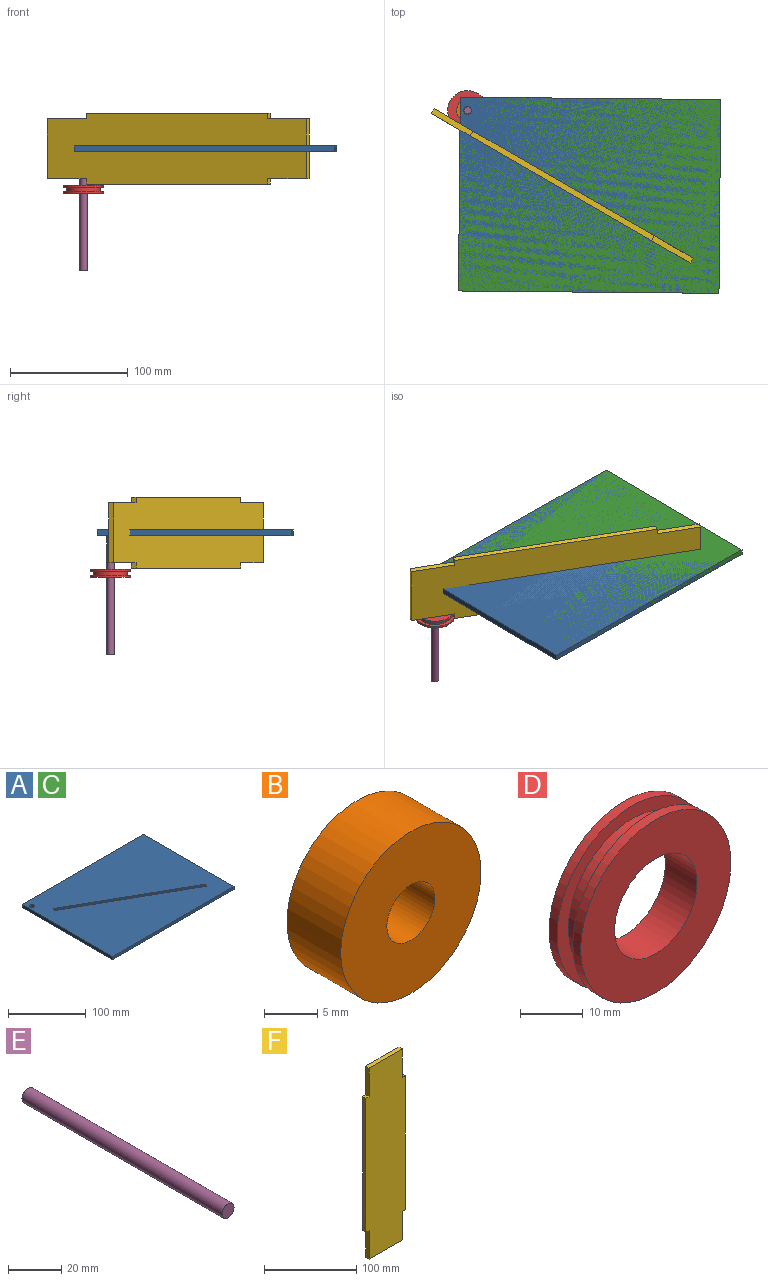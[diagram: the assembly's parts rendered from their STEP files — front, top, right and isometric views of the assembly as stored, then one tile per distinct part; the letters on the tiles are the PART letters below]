
ASSEMBLY  parts=6 mates=3
PART A: 11 faces, bbox 221.1x164.5x4.8 mm
  f0: plane 164.51x4.76mm, normal (1,0,0), area 783.5mm2, adj f1,f6,f9,f10
  f1: plane 221.11x4.76mm, normal (0,1,0), area 1053.1mm2, adj f0,f2,f9,f10
  f2: plane 164.51x4.76mm, normal (-1,0,0), area 783.5mm2, adj f1,f6,f9,f10
  f3: plane 4.76x4.15mm, normal (0.87,-0.49,0), area 22.7mm2, adj f4,f7,f9,f10
  f4: plane 176.89x100mm, normal (-0.49,-0.87,0), area 967.7mm2, adj f3,f5,f9,f10
  f5: plane 4.76x4.15mm, normal (-0.87,0.49,0), area 22.7mm2, adj f4,f7,f9,f10
  f6: plane 221.11x4.76mm, normal (0,-1,0), area 1053.1mm2, adj f0,f2,f9,f10
  f7: plane 176.89x100mm, normal (0.49,0.87,0), area 967.7mm2, adj f3,f5,f9,f10
  f8: cylinder r=3.17mm len=6.35mm, axis (0,0,-1), area 95mm2, adj f9,f10
  f9: plane 221.11x164.51mm, normal (0,0,1), area 35376.1mm2, adj f0,f1,f2,f3,f4,f5,f6,f7
  f10: plane 221.11x164.51mm, normal (0,0,-1), area 35376.1mm2, adj f0,f1,f2,f3,f4,f5,f6,f7
PART B: 4 faces, bbox 18.5x7.1x18.5 mm
  f0: cylinder r=3.17mm len=7.11mm, axis (0,1,0), area 141.9mm2, adj f2,f3
  f1: cylinder r=9.27mm len=18.54mm, axis (0,1,0), area 414.3mm2, adj f2,f3
  f2: plane 18.54x18.54mm, normal (0,-1,0), area 238.4mm2, adj f0,f1
  f3: plane 18.54x18.54mm, normal (0,1,0), area 238.4mm2, adj f0,f1
PART C: same geometry as A
PART D: 8 faces, bbox 33.8x7.1x33.8 mm
  f0: cylinder r=16.89mm len=33.78mm, axis (0,1,0), area 188.7mm2, adj f4,f7
  f1: cylinder r=9.27mm len=18.54mm, axis (0,1,0), area 414.3mm2, adj f3,f4
  f2: cylinder r=16.89mm len=33.78mm, axis (0,1,0), area 188.7mm2, adj f3,f6
  f3: plane 33.78x33.78mm, normal (0,-1,0), area 626.3mm2, adj f1,f2
  f4: plane 33.78x33.78mm, normal (0,1,0), area 626.3mm2, adj f0,f1
  f5: cylinder r=14.35mm len=28.7mm, axis (0,1,0), area 320.6mm2, adj f6,f7
  f6: plane 33.78x33.78mm, normal (0,1,0), area 249.3mm2, adj f2,f5
  f7: plane 33.78x33.78mm, normal (0,-1,0), area 249.3mm2, adj f0,f5
PART E: 3 faces, bbox 6.4x106x6.4 mm
  f0: cylinder r=3.17mm len=106.05mm, axis (0,1,0), area 2115.5mm2, adj f1,f2
  f1: plane 6.35x6.35mm, normal (0,-1,0), area 31.7mm2, adj f0
  f2: plane 6.35x6.35mm, normal (0,1,0), area 31.7mm2, adj f0
PART F: 14 faces, bbox 60.3x4.8x254 mm
  f0: plane 4.76x4.76mm, normal (0,0,-1), area 22.7mm2, adj f1,f11,f12,f13
  f1: plane 38.1x4.76mm, normal (-1,0,0), area 181.5mm2, adj f0,f2,f12,f13
  f2: plane 50.8x4.76mm, normal (0,0,-1), area 241.9mm2, adj f1,f3,f12,f13
  f3: plane 38.1x4.76mm, normal (1,0,0), area 181.5mm2, adj f2,f4,f12,f13
  f4: plane 4.76x4.76mm, normal (0,0,-1), area 22.7mm2, adj f3,f5,f12,f13
  f5: plane 177.8x4.76mm, normal (1,0,0), area 846.8mm2, adj f4,f6,f12,f13
  f6: plane 4.76x4.76mm, normal (0,0,1), area 22.7mm2, adj f5,f7,f12,f13
  f7: plane 38.1x4.76mm, normal (1,0,0), area 181.5mm2, adj f6,f8,f12,f13
  f8: plane 50.8x4.76mm, normal (0,0,1), area 241.9mm2, adj f7,f9,f12,f13
  f9: plane 38.1x4.76mm, normal (-1,0,0), area 181.5mm2, adj f8,f10,f12,f13
  f10: plane 4.76x4.76mm, normal (0,0,1), area 22.7mm2, adj f9,f11,f12,f13
  f11: plane 177.8x4.76mm, normal (-1,0,0), area 846.8mm2, adj f0,f10,f12,f13
  f12: plane 254x60.33mm, normal (0,-1,0), area 14596.7mm2, adj f0,f1,f2,f3,f4,f5,f6,f7
  f13: plane 254x60.33mm, normal (0,1,0), area 14596.7mm2, adj f0,f1,f2,f3,f4,f5,f6,f7
PLACE A rot(axis=(0,0,-1),0.5deg) t=(-457.49,-244.18,4.98)mm
PLACE B rot(axis=(-1,0,0),90deg) t=(-449.75,-90.96,-30.58)mm
PLACE C rot(axis=(0,0,-1),0.5deg) t=(-457.49,-244.18,4.98)mm
PLACE D rot(axis=(-1,0,0),90deg) t=(-449.75,-90.96,-30.58)mm
PLACE E rot(axis=(-1,0,0),90deg) t=(-449.75,-90.96,-96.31)mm
PLACE F rot(axis=(0.25,0.94,-0.25),93.8deg) t=(-445.2,-108.49,7.36)mm
MATE fastened D.f1 <-> B.f1  axis (0,0,-1) through (-449.75,-90.96,-30.58)mm
MATE cylindrical B.f0 <-> E.f0  axis (0,0,-1) through (-449.75,-90.96,-30.58)mm
MATE revolute E.f0 <-> C.f8  axis (0,0,-1) through (-449.75,-90.96,9.74)mm
